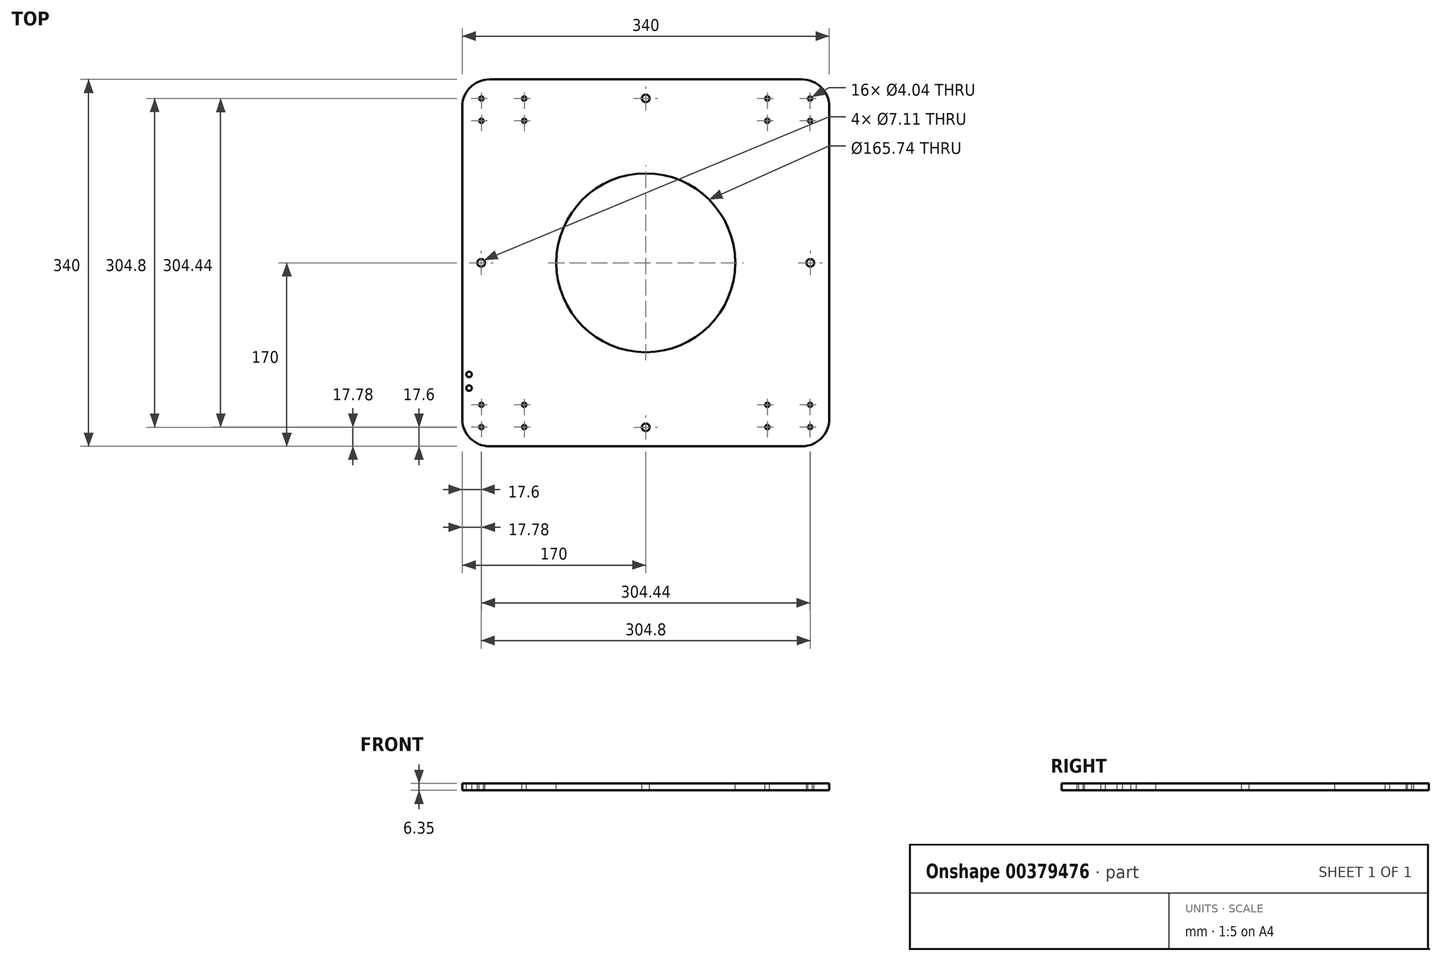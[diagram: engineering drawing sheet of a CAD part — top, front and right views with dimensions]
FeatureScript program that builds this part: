
annotation { "Feature Type Name" : "Feature", "Feature Type Description" : "" }
export const myFeature = defineFeature(function(context is Context, id is Id, definition is map)
    precondition{}
    {
        {
            var Q0;
            Q0=qCreatedBy(makeId("Top.planeOp"),FACE);
            var sketch = newSketch(context, id + "F0", { "sketchPlane" : qUnion([Q0])});
            skLineSegment(sketch, "E0.bottom", {"start": v(-144.6, 170) * mm, "end": v(144.6, 170) * mm});
            skLineSegment(sketch, "E0.top", {"start": v(-144.6, -170) * mm, "end": v(144.6, -170) * mm});
            skLineSegment(sketch, "E0.left", {"start": v(-170, 144.6) * mm, "end": v(-170, -144.6) * mm});
            skLineSegment(sketch, "E0.right", {"start": v(170, 144.6) * mm, "end": v(170, -144.6) * mm});
            skPoint(sketch, "E0.middle", {"position": v(0, 0) * mm});
            skPoint(sketch, "E1.visualSharp", {"position": v(-170, 170) * mm});
            skArc(sketch, "E1.filletArc", {"start": v(-144.6, 170) * mm, "mid": v(-162.56, 162.56) * mm, "end": v(-170, 144.6) * mm});
            skPoint(sketch, "E2.visualSharp", {"position": v(-170, -170) * mm});
            skArc(sketch, "E2.filletArc", {"start": v(-170, -144.6) * mm, "mid": v(-162.56, -162.56) * mm, "end": v(-144.6, -170) * mm});
            skPoint(sketch, "E3.visualSharp", {"position": v(170, -170) * mm});
            skArc(sketch, "E3.filletArc", {"start": v(144.6, -170) * mm, "mid": v(162.56, -162.56) * mm, "end": v(170, -144.6) * mm});
            skPoint(sketch, "E4.visualSharp", {"position": v(170, 170) * mm});
            skArc(sketch, "E4.filletArc", {"start": v(170, 144.6) * mm, "mid": v(162.56, 162.56) * mm, "end": v(144.6, 170) * mm});
            skSolve(sketch);
        }
        {
            var Q0;
            Q0=makeQuery(id+"F0.imprint","IMPRINT",FACE,{"disambiguationData":[TD([[makeQuery(id+"F0.imprint","IMPRINT",EDGE,{"derivedFrom":sQuery(id+"F0.wireOp",EDGE,"E0.bottom")}),-1.0]])]});
            extrude(context, id + "F1", {"entities" : qUnion([Q0]), "depth" : 6.35 * mm});
        }
        {
            var Q0;
            Q0=makeQuery(id+"F1.opExtrude","CAP_FACE",FACE,{"disambiguationData":[OSD([sQuery(id+"F0.wireOp",EDGE,"E0.bottom"),sQuery(id+"F0.wireOp",EDGE,"E0.top"),sQuery(id+"F0.wireOp",EDGE,"E0.left"),sQuery(id+"F0.wireOp",EDGE,"E0.right"),sQuery(id+"F0.wireOp",EDGE,"E1.filletArc"),sQuery(id+"F0.wireOp",EDGE,"E2.filletArc"),sQuery(id+"F0.wireOp",EDGE,"E3.filletArc"),sQuery(id+"F0.wireOp",EDGE,"E4.filletArc")])],"isStart":false});
            var sketch = newSketch(context, id + "F2", { "sketchPlane" : qUnion([Q0])});
            skPoint(sketch, "E5", {"position": v(-112.55, -131.6) * mm});
            skPoint(sketch, "E6", {"position": v(-112.55, -152.22) * mm});
            skPoint(sketch, "E7", {"position": v(-152.22, -152.22) * mm});
            skPoint(sketch, "E8", {"position": v(-152.22, -131.6) * mm});
            skLineSegment(sketch, "E9", {"start": v(0, -170) * mm, "end": v(0, 170) * mm, "construction": true});
            skLineSegment(sketch, "E10", {"start": v(170, 0) * mm, "end": v(-170, 0) * mm, "construction": true});
            skPoint(sketch, "E11.MirrorP", {"position": v(152.22, -152.22) * mm});
            skPoint(sketch, "E12.MirrorP", {"position": v(112.55, -152.22) * mm});
            skPoint(sketch, "E13.MirrorP", {"position": v(112.55, -131.6) * mm});
            skPoint(sketch, "E14.MirrorP", {"position": v(152.22, -131.6) * mm});
            skPoint(sketch, "E15.MirrorP", {"position": v(-152.22, 152.22) * mm});
            skPoint(sketch, "E16.MirrorP", {"position": v(-112.55, 152.22) * mm});
            skPoint(sketch, "E17.MirrorP", {"position": v(-112.55, 131.6) * mm});
            skPoint(sketch, "E18.MirrorP", {"position": v(-152.22, 131.6) * mm});
            skPoint(sketch, "E19.MirrorP", {"position": v(152.22, 131.6) * mm});
            skPoint(sketch, "E20.MirrorP", {"position": v(112.55, 152.22) * mm});
            skPoint(sketch, "E21.MirrorP", {"position": v(112.55, 131.6) * mm});
            skPoint(sketch, "E22.MirrorP", {"position": v(152.22, 152.22) * mm});
            skCircle(sketch, "E23", {"center": v(0, 0) * mm, "radius": 82.87 * mm});
            skPoint(sketch, "E24", {"position": v(-163.65, -103.45) * mm});
            skPoint(sketch, "E25", {"position": v(-163.65, -116.15) * mm});
            skPoint(sketch, "E26", {"position": v(0, 152.4) * mm});
            skPoint(sketch, "E27.1.0", {"position": v(-152.4, 0) * mm});
            skPoint(sketch, "E27.2.0", {"position": v(0, -152.4) * mm});
            skPoint(sketch, "E28.0.3.0", {"position": v(152.4, 0) * mm});
            skSolve(sketch);
        }
        {
            var Q0;
            Q0=makeQuery(id+"F2.imprint","IMPRINT",FACE,{"disambiguationData":[TD([[makeQuery(id+"F2.imprint","IMPRINT",EDGE,{"derivedFrom":sQuery(id+"F2.wireOp",EDGE,"E23")}),1.0]])]});
            extrude(context, id + "F3", {"entities" : qUnion([Q0]), "operationType" : NewBodyOperationType.REMOVE, "endBound" : BoundingType.THROUGH_ALL, "oppositeDirection" : true, "depth" : 25 * mm});
        }
        {
            var Q0;
            Q0=sQuery(id+"F2.wireOp",VERTEX,"E18.MirrorP");
            var Q1;
            Q1=sQuery(id+"F2.wireOp",VERTEX,"E15.MirrorP");
            var Q2;
            Q2=sQuery(id+"F2.wireOp",VERTEX,"E16.MirrorP");
            var Q3;
            Q3=sQuery(id+"F2.wireOp",VERTEX,"E17.MirrorP");
            var Q4;
            Q4=sQuery(id+"F2.wireOp",VERTEX,"E19.MirrorP");
            var Q5;
            Q5=sQuery(id+"F2.wireOp",VERTEX,"E22.MirrorP");
            var Q6;
            Q6=sQuery(id+"F2.wireOp",VERTEX,"E20.MirrorP");
            var Q7;
            Q7=sQuery(id+"F2.wireOp",VERTEX,"E21.MirrorP");
            var Q8;
            Q8=sQuery(id+"F2.wireOp",VERTEX,"E14.MirrorP");
            var Q9;
            Q9=sQuery(id+"F2.wireOp",VERTEX,"E11.MirrorP");
            var Q10;
            Q10=sQuery(id+"F2.wireOp",VERTEX,"E12.MirrorP");
            var Q11;
            Q11=sQuery(id+"F2.wireOp",VERTEX,"E13.MirrorP");
            var Q12;
            Q12=sQuery(id+"F2.wireOp",VERTEX,"E6");
            var Q13;
            Q13=sQuery(id+"F2.wireOp",VERTEX,"E5");
            var Q14;
            Q14=sQuery(id+"F2.wireOp",VERTEX,"E8");
            var Q15;
            Q15=sQuery(id+"F2.wireOp",VERTEX,"E7");
            var Q16;
            Q16=makeQuery(id+"F1.opExtrude","SWEPT_BODY",BODY,{"disambiguationData":[OSD([sQuery(id+"F0.wireOp",EDGE,"E0.bottom"),sQuery(id+"F0.wireOp",EDGE,"E0.top"),sQuery(id+"F0.wireOp",EDGE,"E0.left"),sQuery(id+"F0.wireOp",EDGE,"E0.right"),sQuery(id+"F0.wireOp",EDGE,"E1.filletArc"),sQuery(id+"F0.wireOp",EDGE,"E2.filletArc"),sQuery(id+"F0.wireOp",EDGE,"E3.filletArc"),sQuery(id+"F0.wireOp",EDGE,"E4.filletArc")])]});
            hole(context, id + "F4", {"style" : HoleStyle.SIMPLE, "endStyle" : HoleEndStyle.THROUGH, "standardTappedOrClearance" : lookupTablePath({ "standard" : "ANSI", "size" : "#21 (0.16)", "type" : "Drilled" }), "standardBlindInLast" : lookupTablePath({ "standard" : "ANSI", "size" : "#21", "type" : "Drilled" }), "holeDiameter" : 4.04 * mm, "isTappedThrough" : true, "tappedDepth" : 12 * mm, "tapClearance" : 3, "locations" : qUnion([Q0, Q1, Q2, Q3, Q4, Q5, Q6, Q7, Q8, Q9, Q10, Q11, Q12, Q13, Q14, Q15]), "scope" : qUnion([Q16])});
        }
        {
            var Q0;
            Q0=sQuery(id+"F2.wireOp",VERTEX,"E26");
            var Q1;
            Q1=sQuery(id+"F2.wireOp",VERTEX,"E28.0.3.0");
            var Q2;
            Q2=sQuery(id+"F2.wireOp",VERTEX,"E27.2.0");
            var Q3;
            Q3=sQuery(id+"F2.wireOp",VERTEX,"E27.1.0");
            var Q4;
            Q4=makeQuery(id+"F1.opExtrude","SWEPT_BODY",BODY,{"disambiguationData":[OSD([sQuery(id+"F0.wireOp",EDGE,"E0.bottom"),sQuery(id+"F0.wireOp",EDGE,"E0.top"),sQuery(id+"F0.wireOp",EDGE,"E0.left"),sQuery(id+"F0.wireOp",EDGE,"E0.right"),sQuery(id+"F0.wireOp",EDGE,"E1.filletArc"),sQuery(id+"F0.wireOp",EDGE,"E2.filletArc"),sQuery(id+"F0.wireOp",EDGE,"E3.filletArc"),sQuery(id+"F0.wireOp",EDGE,"E4.filletArc")])]});
            hole(context, id + "F5", {"style" : HoleStyle.SIMPLE, "endStyle" : HoleEndStyle.THROUGH, "holeDiameter" : 7.11 * mm, "isTappedThrough" : true, "tappedDepth" : 12 * mm, "tapClearance" : 3, "locations" : qUnion([Q0, Q1, Q2, Q3]), "scope" : qUnion([Q4])});
        }
        {
            var Q0;
            Q0=sQuery(id+"F2.wireOp",VERTEX,"E25");
            var Q1;
            Q1=sQuery(id+"F2.wireOp",VERTEX,"E24");
            var Q2;
            Q2=makeQuery(id+"F1.opExtrude","SWEPT_BODY",BODY,{"disambiguationData":[OSD([sQuery(id+"F0.wireOp",EDGE,"E0.bottom"),sQuery(id+"F0.wireOp",EDGE,"E0.top"),sQuery(id+"F0.wireOp",EDGE,"E0.left"),sQuery(id+"F0.wireOp",EDGE,"E0.right"),sQuery(id+"F0.wireOp",EDGE,"E1.filletArc"),sQuery(id+"F0.wireOp",EDGE,"E2.filletArc"),sQuery(id+"F0.wireOp",EDGE,"E3.filletArc"),sQuery(id+"F0.wireOp",EDGE,"E4.filletArc")])]});
            hole(context, id + "F6", {"style" : HoleStyle.SIMPLE, "endStyle" : HoleEndStyle.THROUGH, "standardTappedOrClearance" : lookupTablePath({ "standard" : "ANSI", "size" : "#7 (0.2)", "type" : "Drilled" }), "standardBlindInLast" : lookupTablePath({ "standard" : "ANSI", "size" : "#7", "type" : "Drilled" }), "holeDiameter" : 5.1 * mm, "isTappedThrough" : true, "tappedDepth" : 12 * mm, "tapClearance" : 3, "locations" : qUnion([Q0, Q1]), "scope" : qUnion([Q2])});
        }
    });
